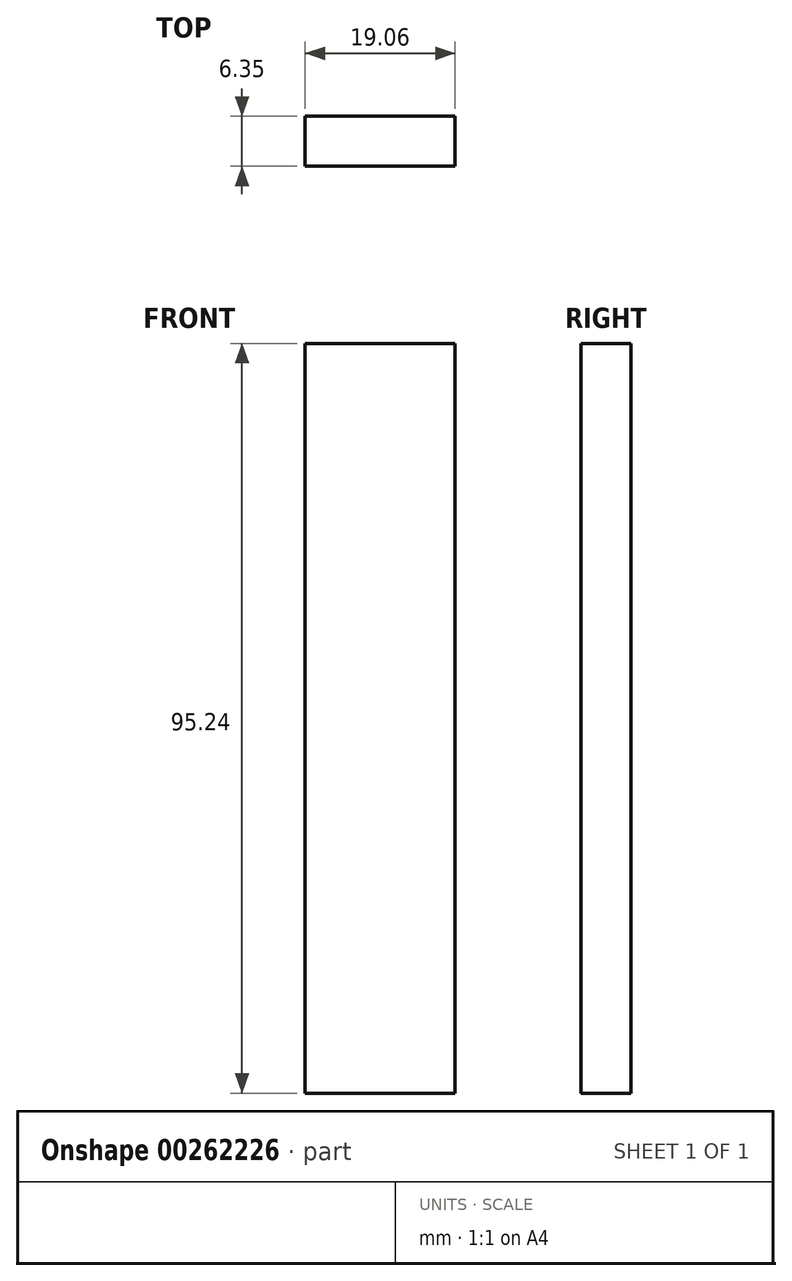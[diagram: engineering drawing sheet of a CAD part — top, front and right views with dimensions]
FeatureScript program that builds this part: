
annotation { "Feature Type Name" : "Feature", "Feature Type Description" : "" }
export const myFeature = defineFeature(function(context is Context, id is Id, definition is map)
    precondition{}
    {
        {
            var Q0;
            Q0=qCreatedBy(makeId("Front.planeOp"),FACE);
            var sketch = newSketch(context, id + "F0", { "sketchPlane" : qUnion([Q0])});
            skLineSegment(sketch, "E0.bottom", {"start": v(-9.52, 47.63) * mm, "end": v(9.53, 47.63) * mm});
            skLineSegment(sketch, "E0.top", {"start": v(-9.53, -47.62) * mm, "end": v(9.52, -47.62) * mm});
            skLineSegment(sketch, "E0.left", {"start": v(-9.53, 47.63) * mm, "end": v(-9.53, -47.62) * mm});
            skLineSegment(sketch, "E0.right", {"start": v(9.53, 47.63) * mm, "end": v(9.52, -47.62) * mm});
            skPoint(sketch, "E0.middle", {"position": v(0, 0) * mm});
            skSolve(sketch);
        }
        {
            var Q0;
            Q0 = qSketchRegion(id + "F0", true);
            extrude(context, id + "F1", {"entities" : qUnion([Q0]), "depth" : 6.35 * mm});
        }
    });
